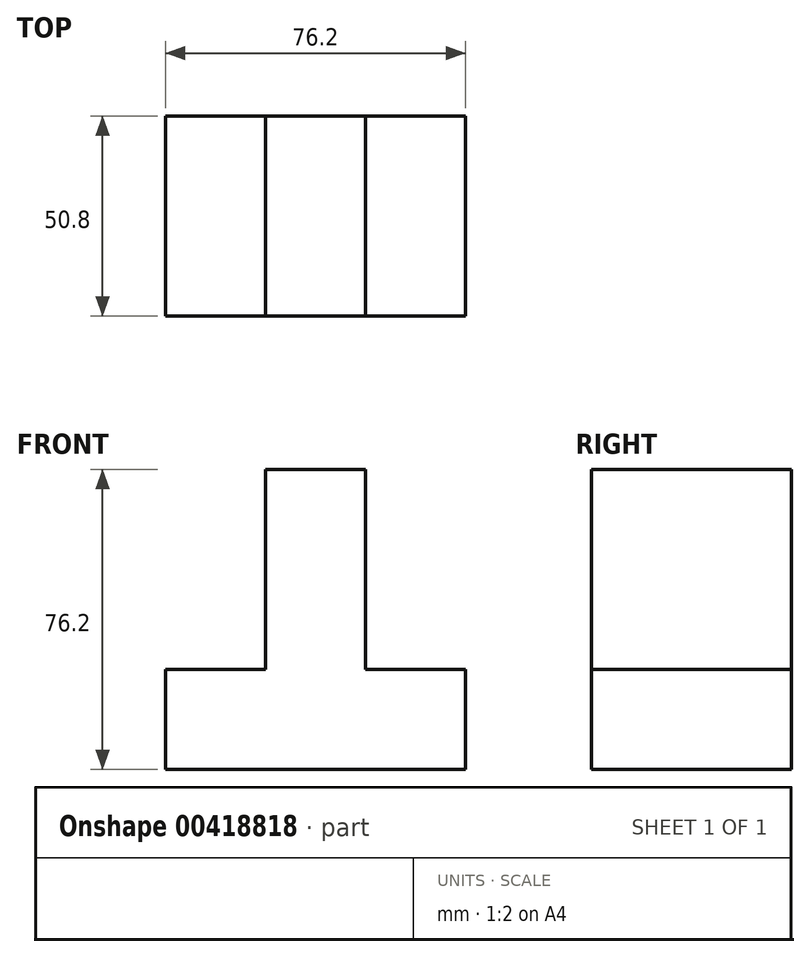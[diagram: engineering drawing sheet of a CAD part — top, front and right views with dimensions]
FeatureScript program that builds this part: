
annotation { "Feature Type Name" : "Feature", "Feature Type Description" : "" }
export const myFeature = defineFeature(function(context is Context, id is Id, definition is map)
    precondition{}
    {
        {
            var Q0;
            Q0=qCreatedBy(makeId("Front.planeOp"),FACE);
            var sketch = newSketch(context, id + "F0", { "sketchPlane" : qUnion([Q0])});
            skLineSegment(sketch, "E0", {"start": v(0, 0) * mm, "end": v(-76.2, 0) * mm});
            skLineSegment(sketch, "E1", {"start": v(-76.2, 0) * mm, "end": v(-76.2, 25.4) * mm});
            skLineSegment(sketch, "E2", {"start": v(-76.2, 25.4) * mm, "end": v(-50.8, 25.4) * mm});
            skLineSegment(sketch, "E3", {"start": v(-50.8, 25.4) * mm, "end": v(-50.8, 76.2) * mm});
            skLineSegment(sketch, "E4", {"start": v(-50.8, 76.2) * mm, "end": v(-25.4, 76.2) * mm});
            skLineSegment(sketch, "E5", {"start": v(-25.4, 76.2) * mm, "end": v(-25.4, 25.4) * mm});
            skLineSegment(sketch, "E6", {"start": v(-25.4, 25.4) * mm, "end": v(0, 25.4) * mm});
            skLineSegment(sketch, "E7", {"start": v(0, 25.4) * mm, "end": v(0, -2.3) * mm});
            skSolve(sketch);
        }
        {
            var Q0;
            {var subQ0=sQuery(id+"F0.wireOp",EDGE,"E0");Q0=makeQuery(id+"F0.imprint","IMPRINT",FACE,{"disambiguationData":[TD([[makeQuery(id+"F0.imprint","IMPRINT",EDGE,{"derivedFrom":subQ0}),-1.0]])]});}
            extrude(context, id + "F1", {"entities" : qUnion([Q0]), "depth" : 50.8 * mm});
        }
    });
